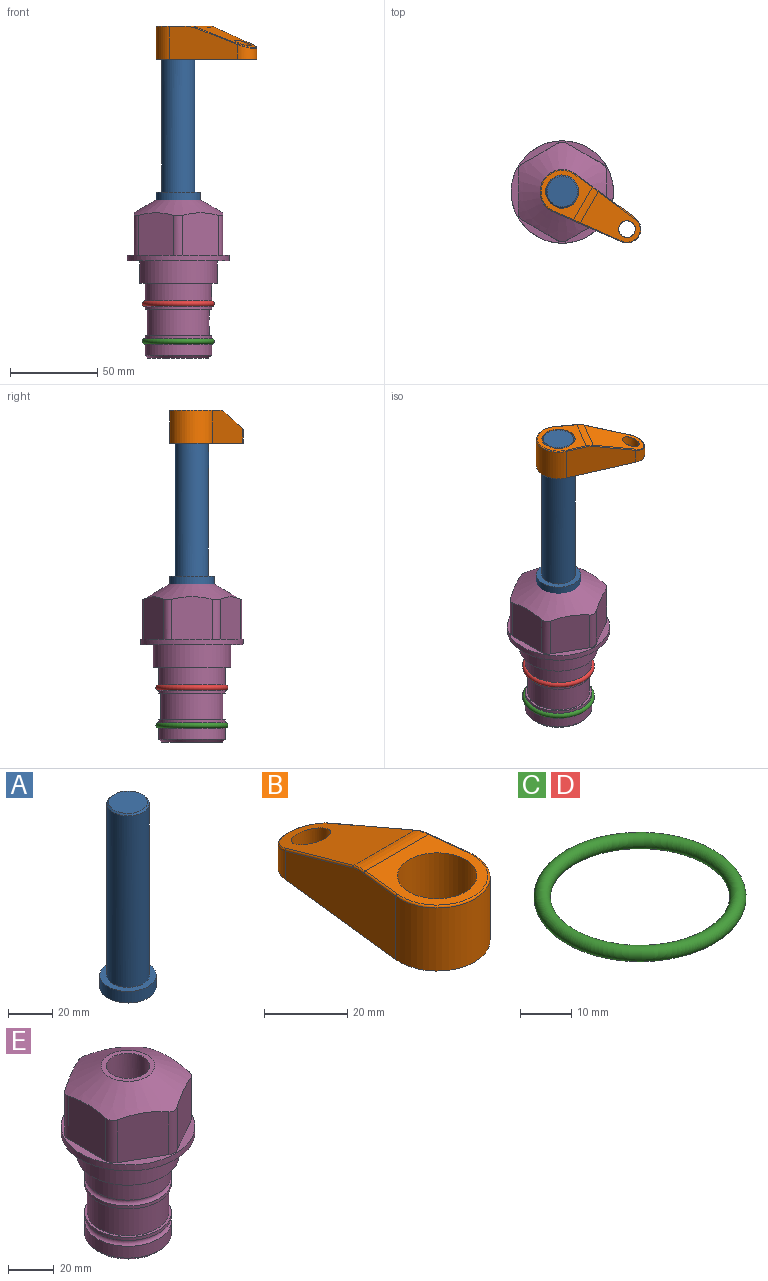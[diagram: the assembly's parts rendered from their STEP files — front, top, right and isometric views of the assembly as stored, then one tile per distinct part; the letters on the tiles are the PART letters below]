
ASSEMBLY  parts=5 mates=3
PART A: 6 faces, bbox 25.4x25.4x101.6 mm
  f0: plane 17.46x17.46mm, normal (0,0,1), area 239.5mm2, adj f5
  f1: plane 25.4x25.4mm, normal (0,0,-1), area 506.7mm2, adj f2
  f2: cylinder r=12.7mm len=25.4mm, axis (0,0,1), area 506.7mm2, adj f1,f3
  f3: plane 25.4x25.4mm, normal (0,0,1), area 221.7mm2, adj f2,f4
  f4: cylinder r=9.53mm len=94.46mm, axis (0,0,1), area 5653mm2, adj f3,f5
  f5: cone r=8.73mm half-angle=45deg, axis (0,0,-1), area 64.4mm2, adj f0,f4
PART B: 44 faces, bbox 27.5x64.5x19.1 mm
  f0: plane 2.3x0.95mm, normal (0,0,-1), area 1mm2, adj f25,f30,f34
  f1: plane 63.5x25.4mm, normal (0,0,-1), area 561.7mm2, adj f2,f3,f4,f5,f6,f7,f19,f20
  f2: cylinder r=12.7mm len=25.4mm, axis (0,0,-1), area 792.2mm2, adj f1,f3,f5,f13
  f3: plane 42.33x18.54mm, normal (0.99,0.11,0), area 647mm2, adj f1,f2,f4,f11,f12,f14
  f4: cylinder r=7.94mm len=15.78mm, axis (0,0,-1), area 158.6mm2, adj f1,f3,f5,f16
  f5: plane 42.33x18.54mm, normal (-0.99,0.11,0), area 647mm2, adj f1,f2,f4,f15,f17,f18
  f6: cylinder r=9.53mm len=19.05mm, axis (0,0,-1), area 1140.1mm2, adj f1,f8
  f7: cylinder r=4.76mm len=10.98mm, axis (0,0,-1), area 276.1mm2, adj f1,f9
  f8: plane 25.83x24.38mm, normal (0,0,1), area 262.2mm2, adj f6,f10,f11,f13,f15
  f9: plane 32.49x20.55mm, normal (0,0.34,0.94), area 489.9mm2, adj f7,f10,f14,f16,f18
  f10: cylinder r=12.7mm len=21.49mm, axis (-1,0,0), area 93.2mm2, adj f8,f9,f12,f17
  f11: cylinder r=0.51mm len=12.34mm, axis (0.11,-0.99,0), area 9.9mm2, adj f3,f8,f12,f13
  f12: bspline ~7.62x1.64mm, area 3.5mm2, adj f3,f10,f11,f14
  f13: torus R=12.19mm, axis (0,0,1), area 33.6mm2, adj f2,f8,f11,f15
  f14: cylinder r=0.51mm len=26.01mm, axis (0.1,-0.93,0.34), area 21.6mm2, adj f3,f9,f12,f16
  f15: cylinder r=0.51mm len=12.34mm, axis (0.11,0.99,0), area 9.9mm2, adj f5,f8,f13,f17
  f16: bspline ~15.78x7.05mm, area 15.7mm2, adj f4,f9,f14,f18
  f17: bspline ~7.62x1.64mm, area 3.5mm2, adj f5,f10,f15,f18
  f18: cylinder r=0.51mm len=26.01mm, axis (0.1,0.93,-0.34), area 21.6mm2, adj f5,f9,f16,f17
  f19: plane 21.6x14.29mm, normal (-0.99,-0.11,0), area 242.6mm2, adj f1,f26,f28,f34,f36,f38
  f20: plane 21.6x14.29mm, normal (0.99,-0.11,0), area 242.6mm2, adj f1,f27,f29,f37,f39,f41
  f21: cylinder r=12.7mm len=14.29mm, axis (0,0,-1), area 173.2mm2, adj f1,f26,f27,f30,f31,f33
  f22: cylinder r=7.94mm len=7.63mm, axis (0,0,-1), area 53.8mm2, adj f1,f28,f29,f42
  f23: plane 2.3x0.95mm, normal (0,0,-1), area 1mm2, adj f25,f33,f37
  f24: plane 17.94x12.32mm, normal (0,-0.34,-0.94), area 191.2mm2, adj f25,f38,f41,f42
  f25: cylinder r=9.53mm len=12.93mm, axis (-1,0,0), area 37.5mm2, adj f0,f23,f24,f31,f36,f39
  f26: cylinder r=1.59mm len=14.29mm, axis (0,0,-1), area 49mm2, adj f1,f19,f21,f32
  f27: cylinder r=1.59mm len=14.29mm, axis (0,0,-1), area 49mm2, adj f1,f20,f21,f35
  f28: cylinder r=1.59mm len=7.28mm, axis (0,0,-1), area 22.1mm2, adj f1,f19,f22,f40
  f29: cylinder r=1.59mm len=7.28mm, axis (0,0,-1), area 22.1mm2, adj f1,f20,f22,f43
  f30: torus R=14.29mm, axis (0,0,1), area 5.8mm2, adj f0,f21,f31,f32
  f31: bspline ~11.06x2.73mm, area 20.8mm2, adj f21,f25,f30,f33
  f32: sphere r=1.59mm, area 5.4mm2, adj f26,f30,f34
  f33: torus R=14.29mm, axis (0,0,1), area 5.8mm2, adj f21,f23,f31,f35
  f34: cylinder r=1.59mm len=1.68mm, axis (-0.11,0.99,0), area 2.4mm2, adj f0,f19,f32,f36
  f35: sphere r=1.59mm, area 5.4mm2, adj f27,f33,f37
  f36: bspline ~5.82x2.33mm, area 7.7mm2, adj f19,f25,f34,f38
  f37: cylinder r=1.59mm len=1.68mm, axis (0.11,0.99,0), area 2.4mm2, adj f20,f23,f35,f39
  f38: cylinder r=1.59mm len=18.33mm, axis (0.1,-0.93,0.34), area 46.7mm2, adj f19,f24,f36,f40
  f39: bspline ~5.82x2.33mm, area 7.7mm2, adj f20,f25,f37,f41
  f40: sphere r=1.59mm, area 3.6mm2, adj f28,f38,f42
  f41: cylinder r=1.59mm len=18.33mm, axis (0.1,0.93,-0.34), area 46.7mm2, adj f20,f24,f39,f43
  f42: bspline ~8.31x1.84mm, area 15.3mm2, adj f22,f24,f40,f43
  f43: sphere r=1.59mm, area 3.6mm2, adj f29,f41,f42
PART C: 1 faces, bbox 44.7x44.7x3.2 mm
  f0: torus R=19.05mm, axis (0,0,1), area 1193.9mm2
PART D: same geometry as C
PART E: 36 faces, bbox 58.7x58.7x91.2 mm
  f0: cylinder r=17.78mm len=35.56mm, axis (0,0,1), area 1670.8mm2, adj f23,f24,f31
  f1: cylinder r=19.05mm len=38.1mm, axis (0,0,1), area 1191.9mm2, adj f26,f27,f30
  f2: plane 58.66x58.66mm, normal (0,0,-1), area 1150.6mm2, adj f3,f28
  f3: cylinder r=29.33mm len=58.66mm, axis (0,0,-1), area 585.1mm2, adj f2,f4
  f4: plane 58.66x58.66mm, normal (0,0,1), area 475.9mm2, adj f3,f5,f6,f7,f8,f9,f10,f11
  f5: plane 24.5x20.32mm, normal (-0.5,0.87,0), area 562.8mm2, adj f4,f15,f16,f17
  f6: plane 24.5x20.32mm, normal (0.5,0.87,0), area 562.8mm2, adj f4,f14,f15,f17
  f7: plane 24.5x23.48mm, normal (1,0,0), area 562.8mm2, adj f4,f13,f14,f17
  f8: plane 24.5x20.32mm, normal (0.5,-0.87,0), area 562.8mm2, adj f4,f12,f13,f17
  f9: plane 24.5x20.32mm, normal (-0.5,-0.87,0), area 562.8mm2, adj f4,f11,f12,f17
  f10: plane 24.5x23.48mm, normal (-1,0,0), area 562.8mm2, adj f4,f11,f16,f17
  f11: cylinder r=5.08mm len=23.01mm, axis (0,0,-1), area 121.2mm2, adj f4,f9,f10,f17
  f12: cylinder r=5.08mm len=23.01mm, axis (0,0,-1), area 121.2mm2, adj f4,f8,f9,f17
  f13: cylinder r=5.08mm len=23.01mm, axis (0,0,-1), area 121.2mm2, adj f4,f7,f8,f17
  f14: cylinder r=5.08mm len=23.01mm, axis (0,0,-1), area 121.2mm2, adj f4,f6,f7,f17
  f15: cylinder r=5.08mm len=23.01mm, axis (0,0,-1), area 121.2mm2, adj f4,f5,f6,f17
  f16: cylinder r=5.08mm len=23.01mm, axis (0,0,-1), area 121.2mm2, adj f4,f5,f10,f17
  f17: cone r=11.73mm half-angle=60deg, axis (0,0,-1), area 2071.8mm2, adj f5,f6,f7,f8,f9,f10,f11,f12
  f18: plane 23.46x23.46mm, normal (0,0,1), area 147.4mm2, adj f17,f35
  f19: plane 34.93x34.93mm, normal (0,0,-1), area 958mm2, adj f29
  f20: cylinder r=19.05mm len=38.1mm, axis (0,0,1), area 760.1mm2, adj f21,f29
  f21: torus R=19.05mm, axis (0,0,1), area 565.3mm2, adj f20,f22
  f22: cylinder r=19.05mm len=38.1mm, axis (0,0,1), area 190mm2, adj f21,f23
  f23: plane 38.1x38.1mm, normal (0,0,1), area 146.9mm2, adj f0,f22
  f24: plane 38.1x38.1mm, normal (0,0,-1), area 146.9mm2, adj f0,f25
  f25: cylinder r=19.05mm len=38.1mm, axis (0,0,1), area 190mm2, adj f24,f26
  f26: torus R=19.05mm, axis (0,0,1), area 565.3mm2, adj f1,f25
  f27: plane 44.45x44.45mm, normal (0,0,-1), area 411.7mm2, adj f1,f28
  f28: cylinder r=22.23mm len=44.45mm, axis (0,0,1), area 1773.5mm2, adj f2,f27
  f29: cone r=19.05mm half-angle=45deg, axis (0,0,1), area 257.5mm2, adj f19,f20
  f30: cylinder r=3.17mm len=6.75mm, axis (-1,0,0), area 128mm2, adj f1,f33
  f31: cylinder r=3.17mm len=6.35mm, axis (-1,0,0), area 102.5mm2, adj f0,f33
  f32: plane 25.4x25.4mm, normal (0,0,1), area 506.7mm2, adj f33
  f33: cylinder r=12.7mm len=66.42mm, axis (0,0,-1), area 5236.2mm2, adj f30,f31,f32,f34
  f34: cone r=9.53mm half-angle=30deg, axis (0,0,-1), area 443.4mm2, adj f33,f35
  f35: cylinder r=9.53mm len=19.05mm, axis (0,0,-1), area 849mm2, adj f18,f34
PLACE A rot(axis=(0,0,-1),30.1deg) t=(0,0,61.07)mm
PLACE B rot(axis=(0,0,-1),120.1deg) t=(0,0,115.68)mm
PLACE C t=(0,0,-21.59)mm
PLACE D at identity
PLACE E at identity fixed
MATE fastened C.f0 <-> E.f0  axis (0,0,1) through (0,0,-46.1)mm
MATE cylindrical A.f2 <-> E.f0  axis (0,0,1) through (0,0,86.71)mm
MATE fastened B.f2 <-> A.f2  axis (0,0,1) through (0,0,134.73)mm
